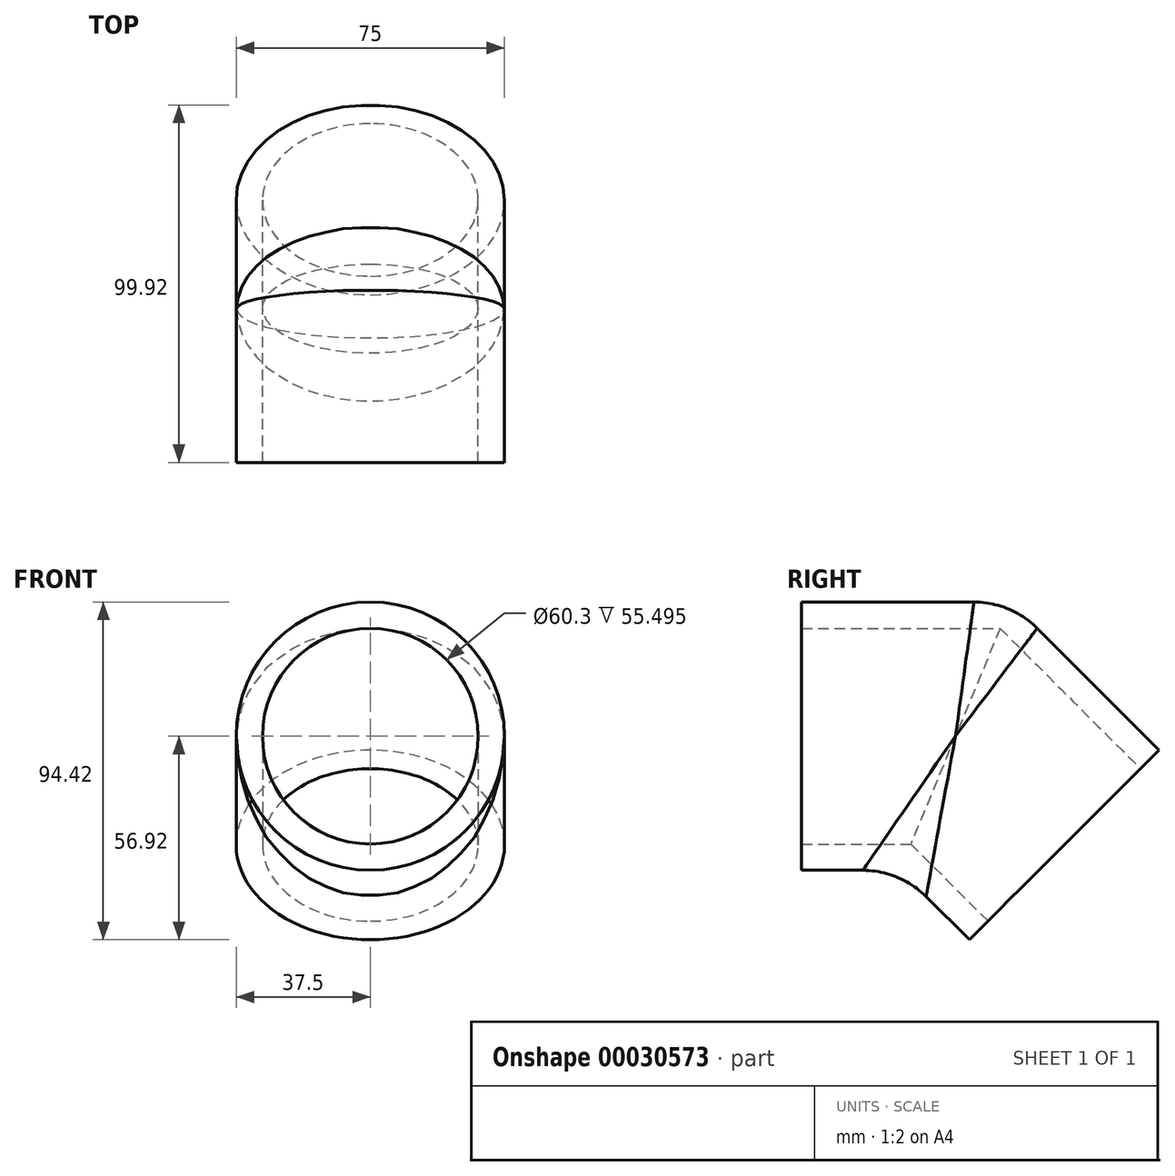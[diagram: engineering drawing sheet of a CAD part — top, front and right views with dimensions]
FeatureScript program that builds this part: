
annotation { "Feature Type Name" : "Feature", "Feature Type Description" : "" }
export const myFeature = defineFeature(function(context is Context, id is Id, definition is map)
    precondition{}
    {
        {
            var Q0;
            Q0=qCreatedBy(makeId("Front.planeOp"),FACE);
            var sketch = newSketch(context, id + "F0", { "sketchPlane" : qUnion([Q0])});
            skCircle(sketch, "E0", {"center": v(0, 37.5) * mm, "radius": 37.5 * mm});
            skCircle(sketch, "E1", {"center": v(0, 37.5) * mm, "radius": 30.15 * mm});
            skSolve(sketch);
        }
        {
            var Q0;
            Q0=qCreatedBy(makeId("Right.planeOp"),FACE);
            var sketch = newSketch(context, id + "F1", { "sketchPlane" : qUnion([Q0])});
            skLineSegment(sketch, "E2", {"start": v(0, 37.5) * mm, "end": v(43, 37.5) * mm});
            skLineSegment(sketch, "E3", {"start": v(43, 37.5) * mm, "end": v(73.4, 7.1) * mm});
            skPoint(sketch, "E4.visualSharp", {"position": v(43, 37.5) * mm});
            skSolve(sketch);
        }
        {
            var Q0;
            Q0=makeQuery(id+"F0.imprint","IMPRINT",FACE,{"disambiguationData":[TD([[makeQuery(id+"F0.imprint","IMPRINT",EDGE,{"derivedFrom":sQuery(id+"F0.wireOp",EDGE,"E0")}),1.0]])]});
            var Q1;
            Q1 = qConstructionFilter(qBodyType(qCreatedBy(id + "F1" ,EDGE), BodyType.WIRE), ConstructionObject.NO);
            sweep(context, id + "F2", {"profiles" : qUnion([Q0]), "path" : qUnion([Q1])});
        }
        {
            var Q0;
            Q0=makeQuery(id+"F2.opSweep","MID_CAP_EDGE",EDGE,{"disambiguationData":[OSD([sQuery(id+"F0.wireOp",EDGE,"E0"),sQuery(id+"F1.wireOp",VERTEX,"E3.start")])],"capPos":1.0});
            fillet(context, id + "F3", {"entities" : qUnion([Q0]), "radius" : 25 * mm, "tangentPropagation" : true, "allowEdgeOverflow" : false});
        }
    });
